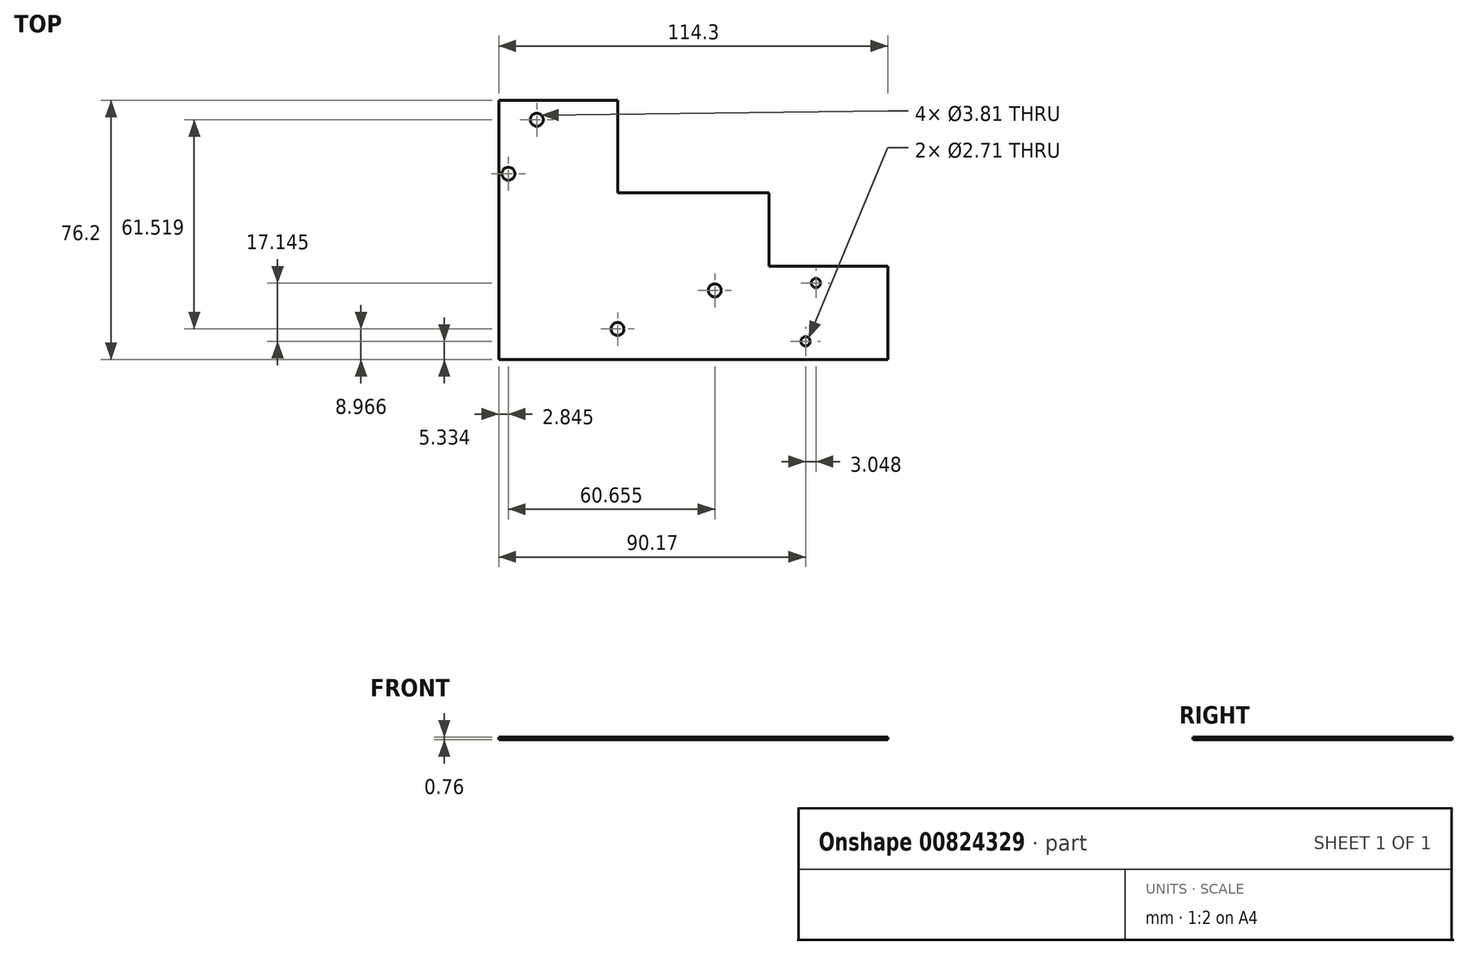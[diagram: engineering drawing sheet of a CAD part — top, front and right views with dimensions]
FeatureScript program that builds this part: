
annotation { "Feature Type Name" : "Feature", "Feature Type Description" : "" }
export const myFeature = defineFeature(function(context is Context, id is Id, definition is map)
    precondition{}
    {
        {
            var Q0;
            Q0=qCreatedBy(makeId("Top.planeOp"),FACE);
            var sketch = newSketch(context, id + "F0", { "sketchPlane" : qUnion([Q0])});
            skLineSegment(sketch, "E0", {"start": v(0, 0) * mm, "end": v(114.3, 0) * mm});
            skLineSegment(sketch, "E1", {"start": v(114.3, 0) * mm, "end": v(114.3, 27.43) * mm});
            skLineSegment(sketch, "E2", {"start": v(114.3, 27.43) * mm, "end": v(79.38, 27.43) * mm});
            skLineSegment(sketch, "E3", {"start": v(79.38, 27.43) * mm, "end": v(79.38, 49.02) * mm});
            skLineSegment(sketch, "E4", {"start": v(79.38, 49.02) * mm, "end": v(34.93, 49.02) * mm});
            skLineSegment(sketch, "E5", {"start": v(34.93, 49.02) * mm, "end": v(34.93, 76.2) * mm});
            skLineSegment(sketch, "E6", {"start": v(34.93, 76.2) * mm, "end": v(0, 76.2) * mm});
            skLineSegment(sketch, "E7", {"start": v(0, 76.2) * mm, "end": v(0, 0) * mm});
            skSolve(sketch);
        }
        {
            var Q0;
            Q0 = qSketchRegion(id + "F0", true);
            extrude(context, id + "F1", {"entities" : qUnion([Q0]), "depth" : 0.76 * mm, "offsetDistance" : 25.4 * mm});
        }
        {
            var Q0;
            Q0=makeQuery(id+"F1.opExtrude","CAP_FACE",FACE,{"disambiguationData":[OSD([sQuery(id+"F0.wireOp",EDGE,"E0"),sQuery(id+"F0.wireOp",EDGE,"E1"),sQuery(id+"F0.wireOp",EDGE,"E2"),sQuery(id+"F0.wireOp",EDGE,"E3"),sQuery(id+"F0.wireOp",EDGE,"E4"),sQuery(id+"F0.wireOp",EDGE,"E5"),sQuery(id+"F0.wireOp",EDGE,"E6"),sQuery(id+"F0.wireOp",EDGE,"E7")])],"isStart":false});
            var sketch = newSketch(context, id + "F2", { "sketchPlane" : qUnion([Q0])});
            skCircle(sketch, "E8", {"center": v(11.2, 70.48) * mm, "radius": 1.9 * mm});
            skCircle(sketch, "E9", {"center": v(2.84, 54.61) * mm, "radius": 1.9 * mm});
            skCircle(sketch, "E10", {"center": v(34.93, 8.97) * mm, "radius": 1.9 * mm});
            skCircle(sketch, "E11", {"center": v(63.5, 20.32) * mm, "radius": 1.9 * mm});
            skSolve(sketch);
        }
        {
            var Q0;
            Q0 = qSketchRegion(id + "F2", true);
            extrude(context, id + "F3", {"entities" : qUnion([Q0]), "operationType" : NewBodyOperationType.REMOVE, "endBound" : BoundingType.THROUGH_ALL, "oppositeDirection" : true, "depth" : 25.4 * mm, "offsetDistance" : 25.4 * mm});
        }
        {
            var Q0;
            Q0=makeQuery(id+"F1.opExtrude","CAP_FACE",FACE,{"disambiguationData":[OSD([sQuery(id+"F0.wireOp",EDGE,"E0"),sQuery(id+"F0.wireOp",EDGE,"E1"),sQuery(id+"F0.wireOp",EDGE,"E2"),sQuery(id+"F0.wireOp",EDGE,"E3"),sQuery(id+"F0.wireOp",EDGE,"E4"),sQuery(id+"F0.wireOp",EDGE,"E5"),sQuery(id+"F0.wireOp",EDGE,"E6"),sQuery(id+"F0.wireOp",EDGE,"E7")])],"isStart":false});
            var sketch = newSketch(context, id + "F4", { "sketchPlane" : qUnion([Q0])});
            skCircle(sketch, "E12", {"center": v(90.17, 5.33) * mm, "radius": 1.35 * mm});
            skCircle(sketch, "E13", {"center": v(93.22, 22.48) * mm, "radius": 1.35 * mm});
            skSolve(sketch);
        }
        {
            var Q0;
            Q0=makeQuery(id+"F4.imprint","IMPRINT",FACE,{"disambiguationData":[TD([[makeQuery(id+"F4.imprint","IMPRINT",EDGE,{"derivedFrom":sQuery(id+"F4.wireOp",EDGE,"E13")}),1.0]])]});
            var Q1;
            Q1=makeQuery(id+"F4.imprint","IMPRINT",FACE,{"disambiguationData":[TD([[makeQuery(id+"F4.imprint","IMPRINT",EDGE,{"derivedFrom":sQuery(id+"F4.wireOp",EDGE,"E12")}),1.0]])]});
            extrude(context, id + "F5", {"entities" : qUnion([Q0, Q1]), "operationType" : NewBodyOperationType.REMOVE, "endBound" : BoundingType.THROUGH_ALL, "oppositeDirection" : true, "depth" : 25.4 * mm, "offsetDistance" : 25.4 * mm});
        }
    });
